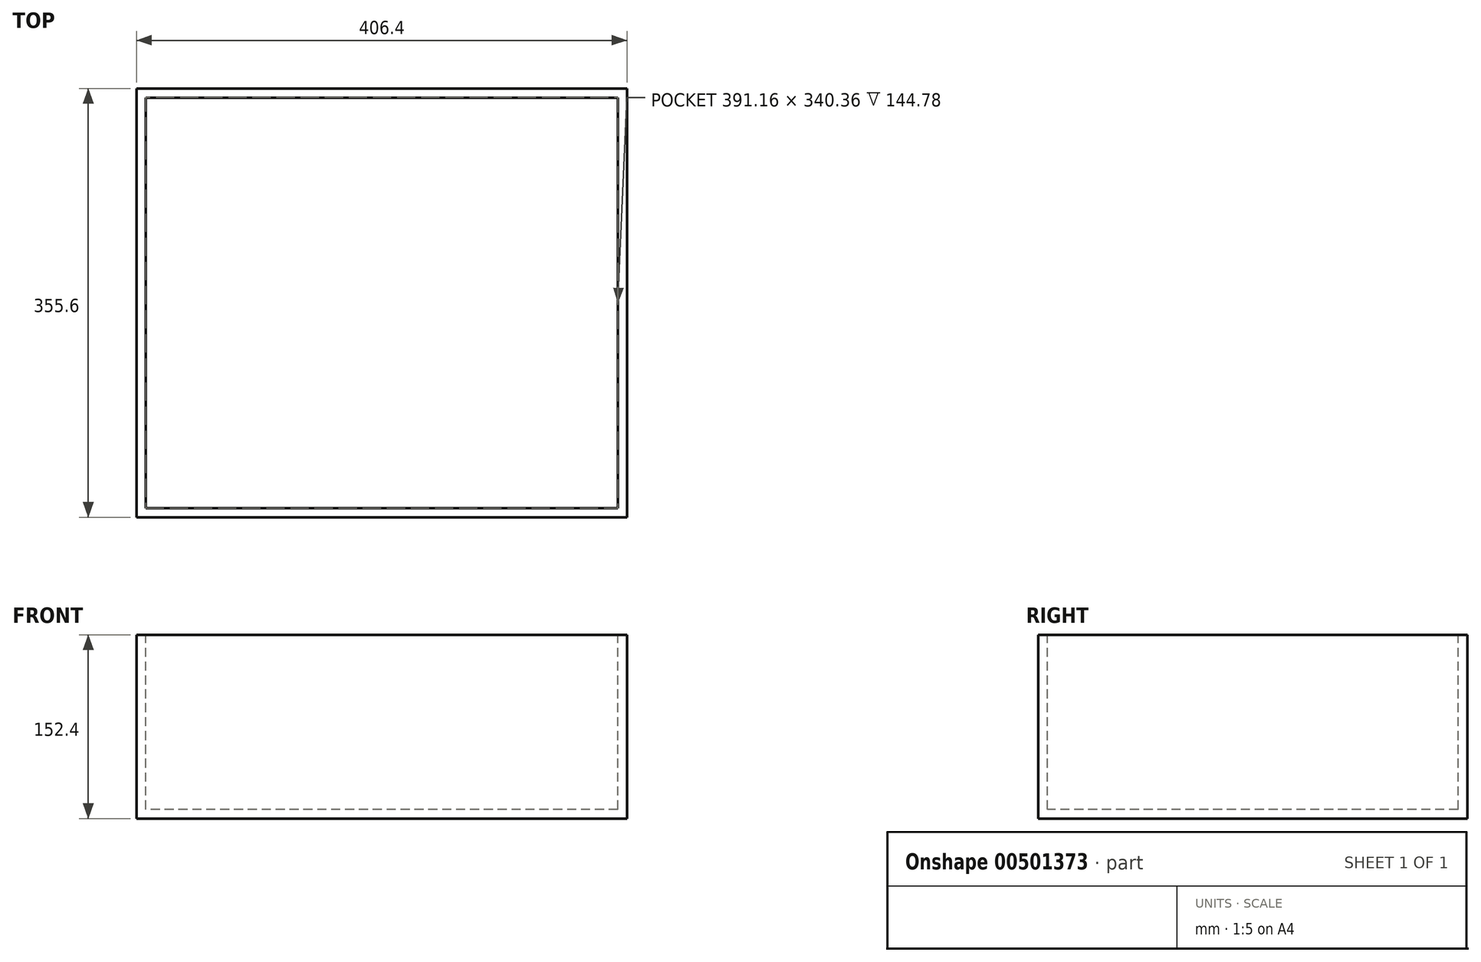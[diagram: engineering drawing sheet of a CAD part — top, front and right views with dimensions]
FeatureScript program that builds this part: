
annotation { "Feature Type Name" : "Feature", "Feature Type Description" : "" }
export const myFeature = defineFeature(function(context is Context, id is Id, definition is map)
    precondition{}
    {
        {
            var Q0;
            Q0=qCreatedBy(makeId("Front.planeOp"),FACE);
            var sketch = newSketch(context, id + "F0", { "sketchPlane" : qUnion([Q0])});
            skLineSegment(sketch, "E0.bottom", {"start": v(203.2, 0) * mm, "end": v(-203.2, 0) * mm});
            skLineSegment(sketch, "E0.top", {"start": v(203.2, 152.4) * mm, "end": v(-203.2, 152.4) * mm});
            skLineSegment(sketch, "E0.left", {"start": v(203.2, 0) * mm, "end": v(203.2, 152.4) * mm});
            skLineSegment(sketch, "E0.right", {"start": v(-203.2, 0) * mm, "end": v(-203.2, 152.4) * mm});
            skLineSegment(sketch, "E1", {"start": v(0, 152.4) * mm, "end": v(0, 0) * mm, "construction": true});
            skSolve(sketch);
        }
        {
            var Q0;
            Q0=qSketchRegion(id+"F0",true);
            extrude(context, id + "F1", {"entities" : qUnion([Q0]), "oppositeDirection" : true, "depth" : 355.6 * mm});
        }
        {
            var Q0;
            Q0=makeQuery(id+"F1.opExtrude","SWEPT_FACE",FACE,{"disambiguationData":[OSD([sQuery(id+"F0.wireOp",EDGE,"E0.top")])]});
            shell(context, id + "F2", {"entities" : qUnion([Q0]), "thickness" : 7.62 * mm});
        }
    });
